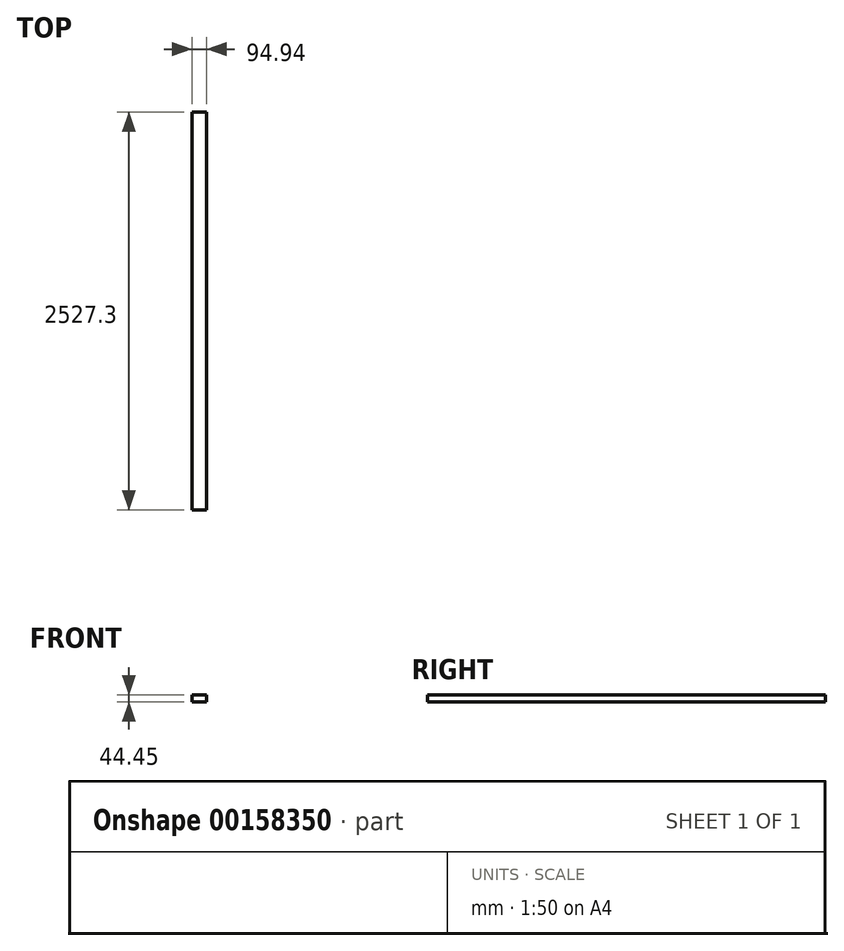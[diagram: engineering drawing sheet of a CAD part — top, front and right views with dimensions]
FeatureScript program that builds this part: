
annotation { "Feature Type Name" : "Feature", "Feature Type Description" : "" }
export const myFeature = defineFeature(function(context is Context, id is Id, definition is map)
    precondition{}
    {
        {
            var Q0;
            Q0=qCreatedBy(makeId("Front.planeOp"),FACE);
            var sketch = newSketch(context, id + "F0", { "sketchPlane" : qUnion([Q0])});
            skLineSegment(sketch, "E0.bottom", {"start": v(-55.96, 32.13) * mm, "end": v(38.98, 32.13) * mm});
            skLineSegment(sketch, "E0.top", {"start": v(-55.96, -12.32) * mm, "end": v(38.98, -12.32) * mm});
            skLineSegment(sketch, "E0.left", {"start": v(-55.96, 32.13) * mm, "end": v(-55.96, -12.32) * mm});
            skLineSegment(sketch, "E0.right", {"start": v(38.98, 32.13) * mm, "end": v(38.98, -12.32) * mm});
            skSolve(sketch);
        }
        {
            var Q0;
            Q0=makeQuery(id+"F0.imprint","IMPRINT",FACE,{"disambiguationData":[TD([[makeQuery(id+"F0.imprint","IMPRINT",EDGE,{"derivedFrom":sQuery(id+"F0.wireOp",EDGE,"E0.bottom")}),-1.0]])]});
            extrude(context, id + "F1", {"entities" : qUnion([Q0]), "endBound" : BoundingType.SYMMETRIC, "depth" : 2527.3 * mm});
        }
    });
